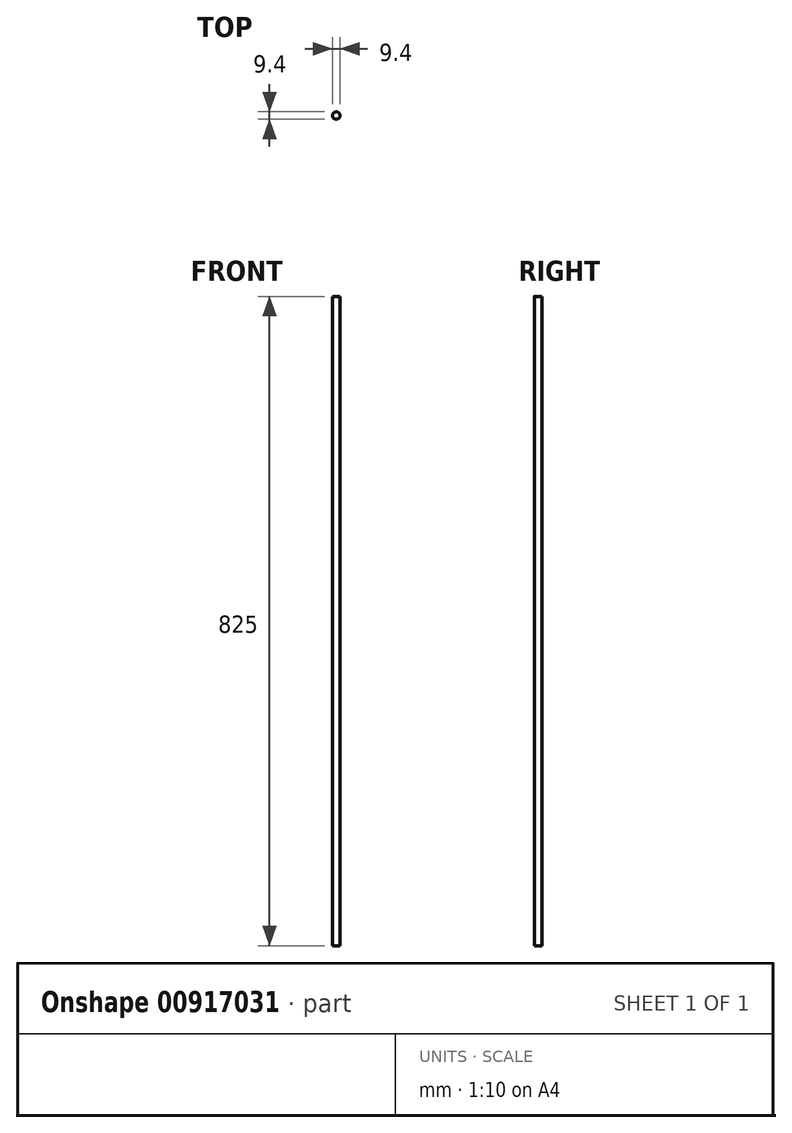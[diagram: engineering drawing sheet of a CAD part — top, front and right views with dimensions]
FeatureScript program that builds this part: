
annotation { "Feature Type Name" : "Feature", "Feature Type Description" : "" }
export const myFeature = defineFeature(function(context is Context, id is Id, definition is map)
    precondition{}
    {
        {
            var Q0;
            Q0=qCreatedBy(makeId("Top.planeOp"),FACE);
            var sketch = newSketch(context, id + "F0", { "sketchPlane" : qUnion([Q0])});
            skCircle(sketch, "E0", {"center": v(0, 0) * mm, "radius": 4.7 * mm});
            skSolve(sketch);
        }
        {
            var Q0;
            Q0=makeQuery(id+"F0.imprint","IMPRINT",FACE,{"disambiguationData":[TD([[makeQuery(id+"F0.imprint","IMPRINT",EDGE,{"derivedFrom":sQuery(id+"F0.wireOp",EDGE,"E0")}),1.0]])]});
            extrude(context, id + "F1", {"entities" : qUnion([Q0]), "depth" : 825 * mm, "offsetDistance" : 25 * mm});
        }
    });
